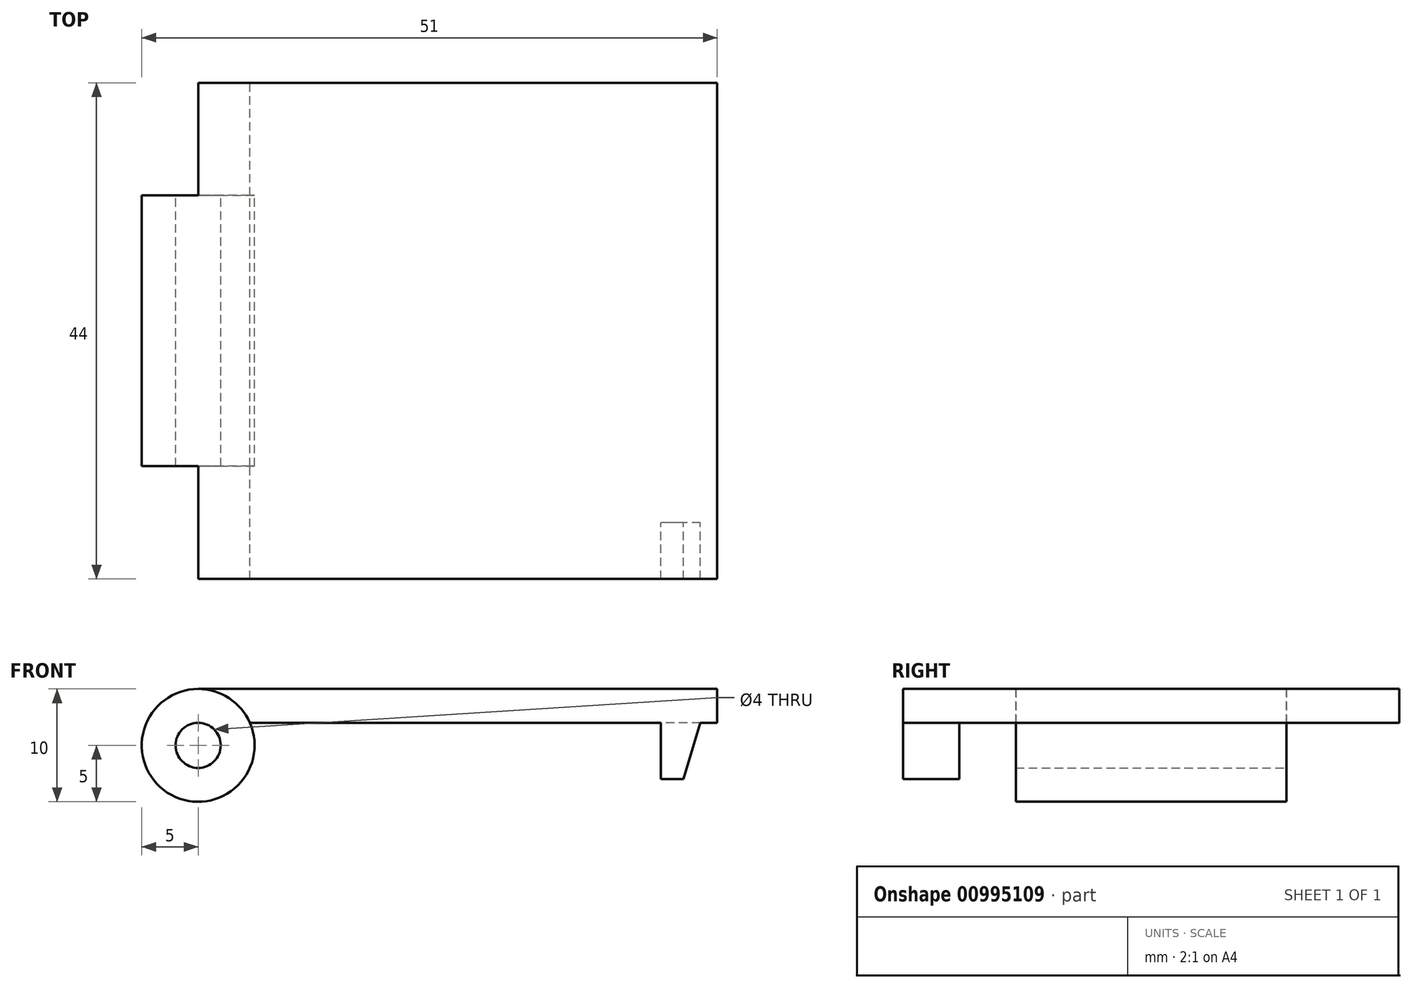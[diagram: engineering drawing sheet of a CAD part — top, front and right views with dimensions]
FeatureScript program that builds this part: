
annotation { "Feature Type Name" : "Feature", "Feature Type Description" : "" }
export const myFeature = defineFeature(function(context is Context, id is Id, definition is map)
    precondition{}
    {
        {
            var Q0;
            Q0=qCreatedBy(makeId("Front.planeOp"),FACE);
            var sketch = newSketch(context, id + "F0", { "sketchPlane" : qUnion([Q0])});
            skLineSegment(sketch, "E0.bottom", {"start": v(-23, 1.5) * mm, "end": v(23, 1.5) * mm});
            skLineSegment(sketch, "E0.top", {"start": v(-23, -1.5) * mm, "end": v(23, -1.5) * mm});
            skLineSegment(sketch, "E0.left", {"start": v(-23, 1.5) * mm, "end": v(-23, -1.5) * mm});
            skLineSegment(sketch, "E0.right", {"start": v(23, 1.5) * mm, "end": v(23, -1.5) * mm});
            skPoint(sketch, "E0.middle", {"position": v(0, 0) * mm});
            skSolve(sketch);
        }
        {
            var Q0;
            Q0 = qSketchRegion(id + "F0", true);
            extrude(context, id + "F1", {"entities" : qUnion([Q0]), "endBound" : BoundingType.SYMMETRIC, "depth" : 44 * mm, "offsetDistance" : 25 * mm});
        }
        {
            var Q0;
            Q0=qCreatedBy(makeId("Front.planeOp"),FACE);
            var sketch = newSketch(context, id + "F2", { "sketchPlane" : qUnion([Q0])});
            skCircle(sketch, "E1", {"center": v(-23, -3.5) * mm, "radius": 5 * mm});
            skCircle(sketch, "E2", {"center": v(-23, -3.5) * mm, "radius": 2 * mm});
            skSolve(sketch);
        }
        {
            var Q0;
            Q0 = qSketchRegion(id + "F2", true);
            extrude(context, id + "F3", {"entities" : qUnion([Q0]), "operationType" : NewBodyOperationType.REMOVE, "endBound" : BoundingType.THROUGH_ALL, "depth" : 25 * mm, "offsetDistance" : 25 * mm, "hasSecondDirection" : true, "secondDirectionBound" : SecondDirectionBoundingType.THROUGH_ALL, "secondDirectionOppositeDirection" : true, "secondDirectionDepth" : 25 * mm});
        }
        {
            var Q0;
            Q0 = qSketchRegion(id + "F2", true);
            extrude(context, id + "F4", {"entities" : qUnion([Q0]), "operationType" : NewBodyOperationType.ADD, "endBound" : BoundingType.SYMMETRIC, "depth" : 24 * mm, "offsetDistance" : 25 * mm});
        }
        {
            var Q0;
            Q0=makeQuery(id+"F1.opExtrude","SWEPT_FACE",FACE,{"disambiguationData":[OSD([sQuery(id+"F0.wireOp",EDGE,"E0.top")])]});
            var sketch = newSketch(context, id + "F5", { "sketchPlane" : qUnion([Q0])});
            skLineSegment(sketch, "E3.bottom", {"start": v(23, 22) * mm, "end": v(18, 22) * mm});
            skLineSegment(sketch, "E3.top", {"start": v(23, 17) * mm, "end": v(18, 17) * mm});
            skLineSegment(sketch, "E3.left", {"start": v(23, 22) * mm, "end": v(23, 17) * mm});
            skLineSegment(sketch, "E3.right", {"start": v(18, 22) * mm, "end": v(18, 17) * mm});
            skSolve(sketch);
        }
        {
            var Q0;
            Q0=makeQuery(id+"F5.imprint","IMPRINT",FACE,{"disambiguationData":[TD([[makeQuery(id+"F5.imprint","IMPRINT",EDGE,{"derivedFrom":sQuery(id+"F5.wireOp",EDGE,"E3.bottom")}),-1.0]])]});
            extrude(context, id + "F6", {"entities" : qUnion([Q0]), "operationType" : NewBodyOperationType.ADD, "depth" : 5 * mm, "offsetDistance" : 25 * mm});
        }
        {
            var Q0;
            Q0=makeQuery(id+"F6.opExtrude","SWEPT_FACE",FACE,{"disambiguationData":[OSD([sQuery(id+"F5.wireOp",EDGE,"E3.top")])]});
            var sketch = newSketch(context, id + "F7", { "sketchPlane" : qUnion([Q0])});
            skLineSegment(sketch, "E4", {"start": v(-23, -6.5) * mm, "end": v(-23, -1.5) * mm});
            skLineSegment(sketch, "E5", {"start": v(-23, -1.5) * mm, "end": v(-21.5, -1.5) * mm});
            skLineSegment(sketch, "E6", {"start": v(-21.5, -1.5) * mm, "end": v(-20, -6.5) * mm});
            skLineSegment(sketch, "E7", {"start": v(-20, -6.5) * mm, "end": v(-23, -6.5) * mm});
            skSolve(sketch);
        }
        {
            var Q0;
            Q0 = qSketchRegion(id + "F7", true);
            extrude(context, id + "F8", {"entities" : qUnion([Q0]), "operationType" : NewBodyOperationType.REMOVE, "endBound" : BoundingType.THROUGH_ALL, "oppositeDirection" : true, "depth" : 25 * mm, "offsetDistance" : 25 * mm});
        }
    });
